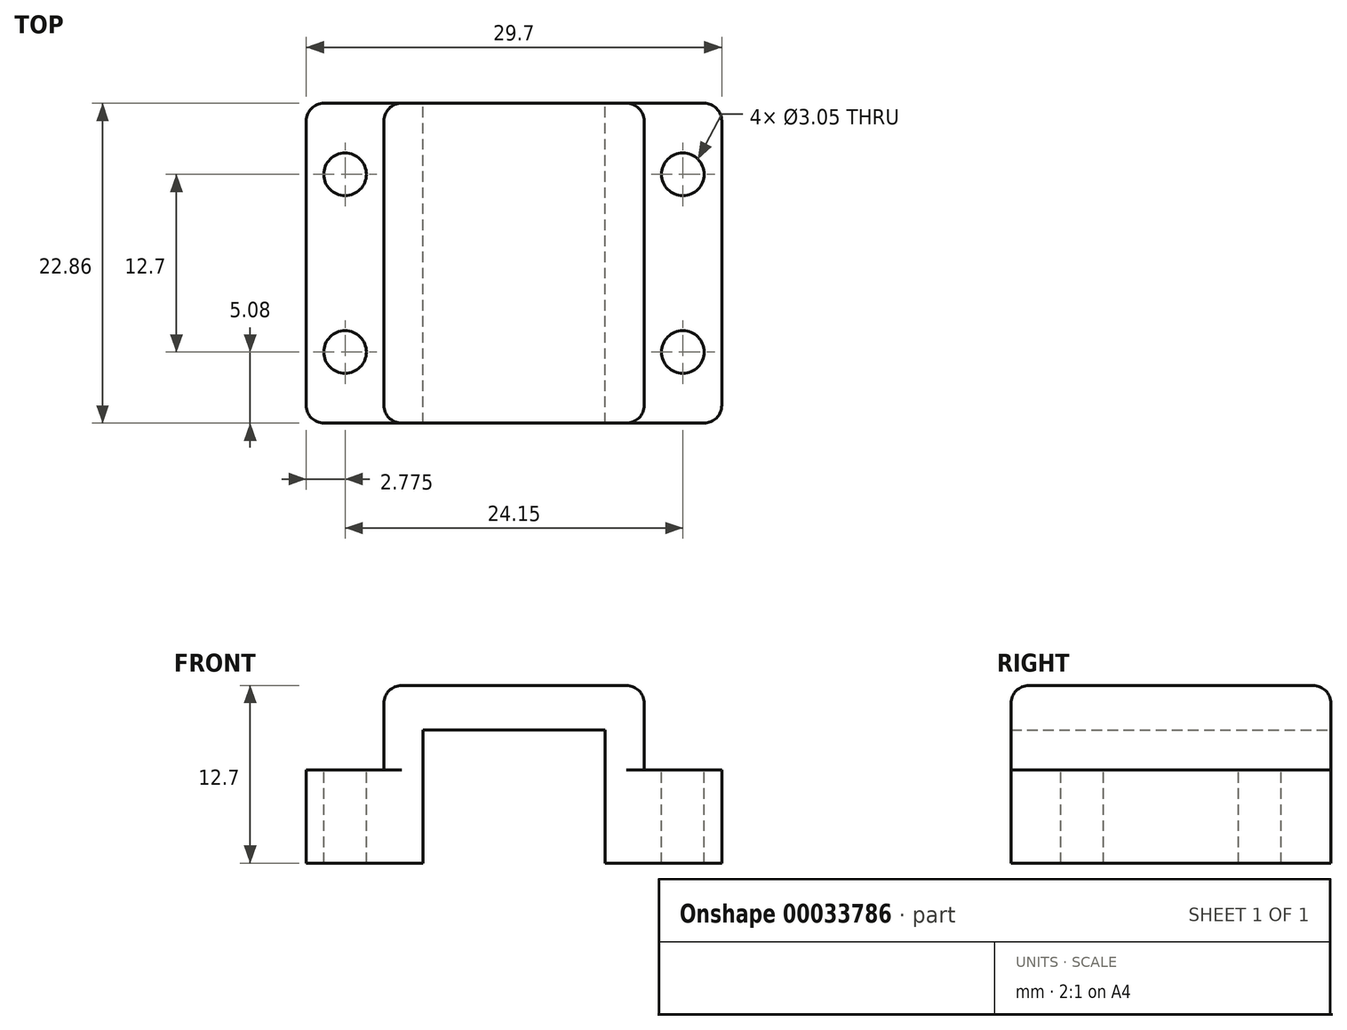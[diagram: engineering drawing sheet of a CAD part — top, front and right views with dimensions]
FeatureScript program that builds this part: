
annotation { "Feature Type Name" : "Feature", "Feature Type Description" : "" }
export const myFeature = defineFeature(function(context is Context, id is Id, definition is map)
    precondition{}
    {
        {
            var Q0;
            Q0=qCreatedBy(makeId("Front.planeOp"),FACE);
            var sketch = newSketch(context, id + "F0", { "sketchPlane" : qUnion([Q0])});
            skLineSegment(sketch, "E0", {"start": v(-14.85, 0) * mm, "end": v(-6.5, 0) * mm});
            skLineSegment(sketch, "E1", {"start": v(-6.5, 0) * mm, "end": v(-6.5, 9.52) * mm});
            skLineSegment(sketch, "E2", {"start": v(-6.5, 9.52) * mm, "end": v(0, 9.52) * mm});
            skLineSegment(sketch, "E3", {"start": v(0, 9.52) * mm, "end": v(0, 12.7) * mm});
            skLineSegment(sketch, "E4", {"start": v(0, 12.7) * mm, "end": v(-9.3, 12.7) * mm});
            skLineSegment(sketch, "E5", {"start": v(-9.3, 12.7) * mm, "end": v(-9.3, 6.65) * mm});
            skLineSegment(sketch, "E6", {"start": v(-9.3, 6.65) * mm, "end": v(-14.85, 6.65) * mm});
            skLineSegment(sketch, "E7", {"start": v(-14.85, 6.65) * mm, "end": v(-14.85, 0) * mm});
            skLineSegment(sketch, "E8.MirrorCS", {"start": v(14.85, 0) * mm, "end": v(6.5, 0) * mm});
            skLineSegment(sketch, "E9.MirrorCS", {"start": v(6.5, 0) * mm, "end": v(6.5, 9.52) * mm});
            skLineSegment(sketch, "E10.MirrorCS", {"start": v(9.3, 12.7) * mm, "end": v(9.3, 6.65) * mm});
            skLineSegment(sketch, "E11.MirrorCS", {"start": v(0, 12.7) * mm, "end": v(9.3, 12.7) * mm});
            skLineSegment(sketch, "E12.MirrorCS", {"start": v(14.85, 6.65) * mm, "end": v(14.85, 0) * mm});
            skLineSegment(sketch, "E13.MirrorCS", {"start": v(9.3, 6.65) * mm, "end": v(14.85, 6.65) * mm});
            skLineSegment(sketch, "E14.MirrorCS", {"start": v(6.5, 9.52) * mm, "end": v(0, 9.52) * mm});
            skLineSegment(sketch, "E15", {"start": v(-14.85, 2.54) * mm, "end": v(0, 2.54) * mm, "construction": true});
            skSolve(sketch);
        }
        {
            var Q0;
            Q0 = qSketchRegion(id + "F0", true);
            extrude(context, id + "F1", {"entities" : qUnion([Q0]), "depth" : 22.86 * mm});
        }
        {
            var Q0;
            Q0=makeQuery(id+"F1.opExtrude","SWEPT_EDGE",EDGE,{"disambiguationData":[OSD([sQuery(id+"F0.wireOp",EDGE,"E10.MirrorCS"),sQuery(id+"F0.wireOp",EDGE,"E11.MirrorCS")])]});
            var Q1;
            Q1=makeQuery(id+"F1.opExtrude","SWEPT_EDGE",EDGE,{"disambiguationData":[OSD([sQuery(id+"F0.wireOp",EDGE,"E4"),sQuery(id+"F0.wireOp",EDGE,"E5")])]});
            fillet(context, id + "F2", {"entities" : qUnion([Q0, Q1]), "radius" : 1.27 * mm, "tangentPropagation" : true, "allowEdgeOverflow" : false});
        }
        {
            var Q0;
            Q0=makeQuery(id+"F1.opExtrude","SWEPT_FACE",FACE,{"disambiguationData":[OSD([sQuery(id+"F0.wireOp",EDGE,"E6")])]});
            var sketch = newSketch(context, id + "F3", { "sketchPlane" : qUnion([Q0])});
            skLineSegment(sketch, "E16", {"start": v(-12.07, 0) * mm, "end": v(-12.07, -22.86) * mm});
            skCircle(sketch, "E17", {"center": v(-12.07, -5.08) * mm, "radius": 1.52 * mm});
            skCircle(sketch, "E18", {"center": v(-12.07, -17.78) * mm, "radius": 1.52 * mm});
            skLineSegment(sketch, "E19", {"start": v(-12.07, -11.43) * mm, "end": v(-14.85, -11.43) * mm});
            skLineSegment(sketch, "E20", {"start": v(-12.07, -5.08) * mm, "end": v(-12.07, -17.78) * mm});
            skCircle(sketch, "E21.MirrorC", {"center": v(12.08, -5.08) * mm, "radius": 1.52 * mm});
            skCircle(sketch, "E22.MirrorC", {"center": v(12.08, -17.78) * mm, "radius": 1.52 * mm});
            skSolve(sketch);
        }
        {
            var Q0;
            Q0 = qSketchRegion(id + "F3", true);
            extrude(context, id + "F4", {"entities" : qUnion([Q0]), "operationType" : NewBodyOperationType.REMOVE, "endBound" : BoundingType.UP_TO_NEXT, "oppositeDirection" : true, "depth" : 25.4 * mm});
        }
        {
            var Q0;
            Q0=makeQuery(id+"F1.opExtrude","CAP_EDGE",EDGE,{"disambiguationData":[OSD([sQuery(id+"F0.wireOp",EDGE,"E12.MirrorCS")])],"isStart":true});
            var Q1;
            Q1=makeQuery(id+"F1.opExtrude","CAP_EDGE",EDGE,{"disambiguationData":[OSD([sQuery(id+"F0.wireOp",EDGE,"E10.MirrorCS")])],"isStart":true});
            var Q2;
            Q2=makeQuery(id+"F1.opExtrude","CAP_EDGE",EDGE,{"disambiguationData":[OSD([sQuery(id+"F0.wireOp",EDGE,"E7")])],"isStart":true});
            var Q3;
            Q3=makeQuery(id+"F1.opExtrude","CAP_EDGE",EDGE,{"disambiguationData":[OSD([sQuery(id+"F0.wireOp",EDGE,"E5")])],"isStart":false});
            var Q4;
            Q4=makeQuery(id+"F1.opExtrude","CAP_EDGE",EDGE,{"disambiguationData":[OSD([sQuery(id+"F0.wireOp",EDGE,"E7")])],"isStart":false});
            var Q5;
            Q5=makeQuery(id+"F1.opExtrude","CAP_EDGE",EDGE,{"disambiguationData":[OSD([sQuery(id+"F0.wireOp",EDGE,"E12.MirrorCS")])],"isStart":false});
            fillet(context, id + "F5", {"entities" : qUnion([Q0, Q1, Q2, Q3, Q4, Q5]), "radius" : 1.27 * mm, "tangentPropagation" : true, "allowEdgeOverflow" : false});
        }
    });
